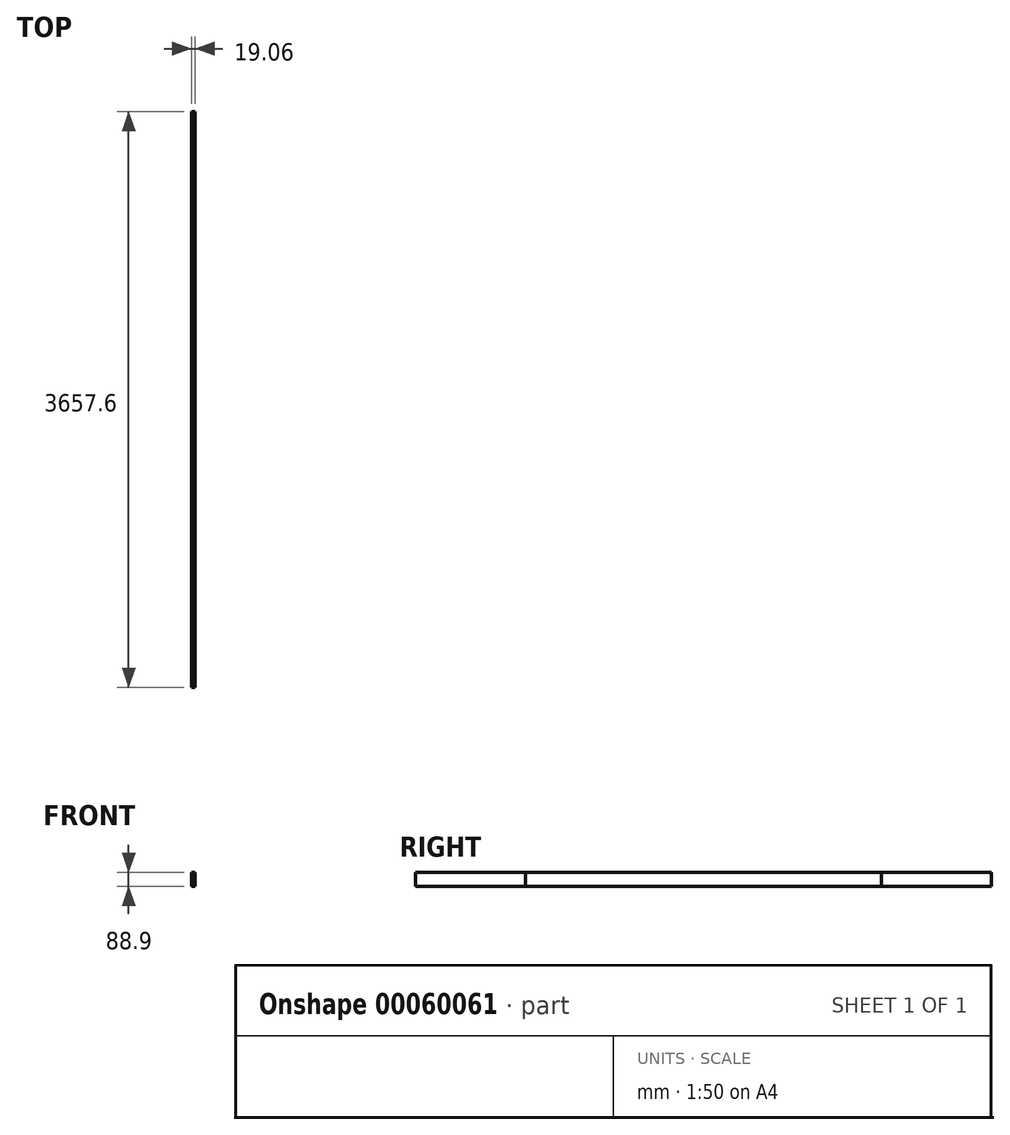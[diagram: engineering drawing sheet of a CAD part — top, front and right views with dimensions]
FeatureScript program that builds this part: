
annotation { "Feature Type Name" : "Feature", "Feature Type Description" : "" }
export const myFeature = defineFeature(function(context is Context, id is Id, definition is map)
    precondition{}
    {
        {
            var Q0;
            Q0=qCreatedBy(makeId("Front.planeOp"),FACE);
            var sketch = newSketch(context, id + "F0", { "sketchPlane" : qUnion([Q0])});
            skLineSegment(sketch, "E0", {"start": v(0, 0) * mm, "end": v(0, 96.35) * mm, "construction": true});
            skLineSegment(sketch, "E1", {"start": v(129.2, 0) * mm, "end": v(0, 0) * mm, "construction": true});
            skLineSegment(sketch, "E2.bottom", {"start": v(-9.53, 44.45) * mm, "end": v(9.53, 44.45) * mm});
            skLineSegment(sketch, "E2.top", {"start": v(-9.53, -44.45) * mm, "end": v(9.53, -44.45) * mm});
            skLineSegment(sketch, "E2.left", {"start": v(-9.53, 44.45) * mm, "end": v(-9.53, -44.45) * mm});
            skLineSegment(sketch, "E2.right", {"start": v(9.53, 44.45) * mm, "end": v(9.52, -44.45) * mm});
            skSolve(sketch);
        }
        {
            var Q0;
            Q0=makeQuery(id+"F0.imprint","IMPRINT",FACE,{"disambiguationData":[TD([[makeQuery(id+"F0.imprint","IMPRINT",EDGE,{"derivedFrom":sQuery(id+"F0.wireOp",EDGE,"E2.bottom")}),-1.0]])]});
            extrude(context, id + "F1", {"entities" : qUnion([Q0]), "endBound" : BoundingType.SYMMETRIC, "depth" : 2260.6 * mm});
        }
        {
            var Q0;
            Q0 = qSketchRegion(id + "F0", true);
            extrude(context, id + "F2", {"entities" : qUnion([Q0]), "endBound" : BoundingType.SYMMETRIC, "depth" : 3657.6 * mm});
        }
    });
